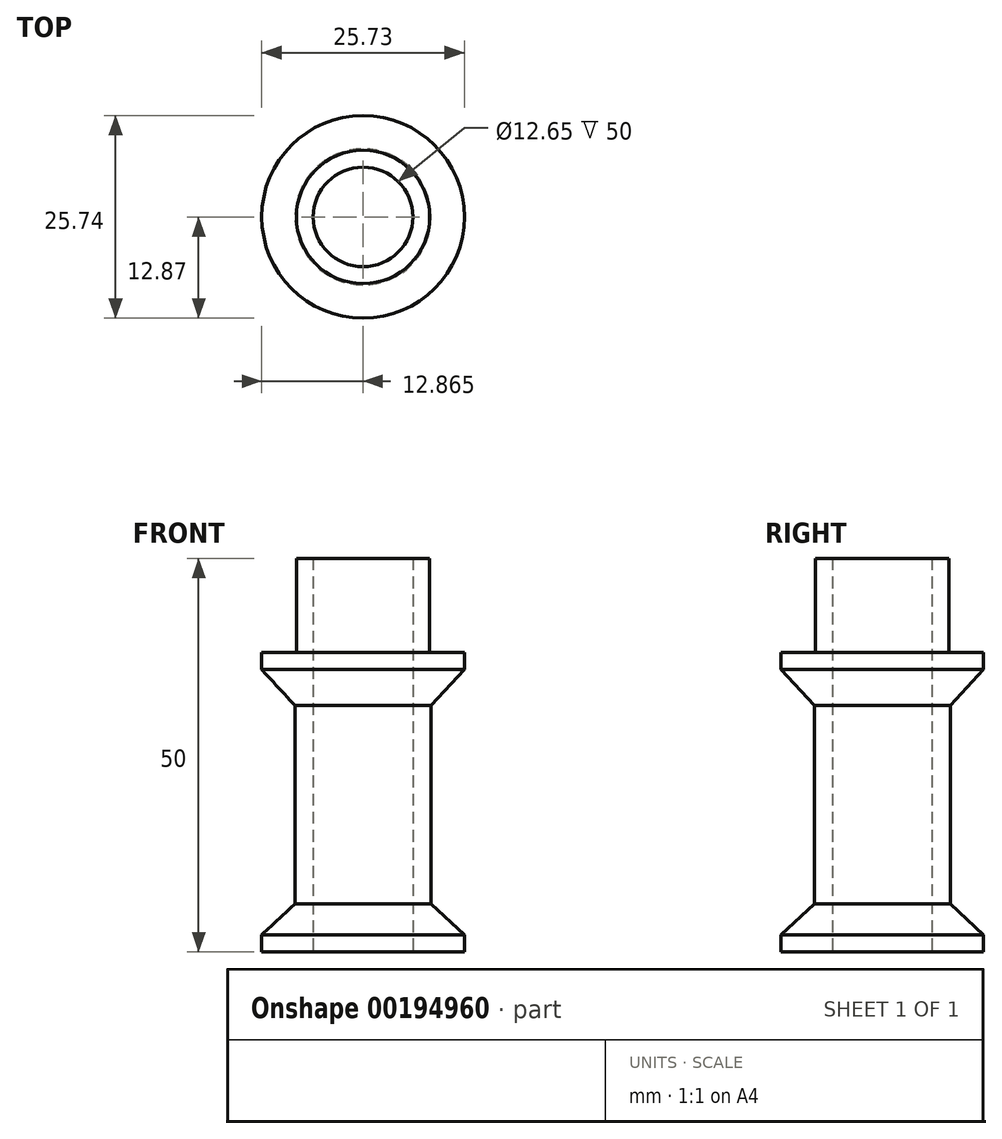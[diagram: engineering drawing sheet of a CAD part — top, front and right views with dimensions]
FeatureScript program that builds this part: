
annotation { "Feature Type Name" : "Feature", "Feature Type Description" : "" }
export const myFeature = defineFeature(function(context is Context, id is Id, definition is map)
    precondition{}
    {
        {
            var Q0;
            Q0=qCreatedBy(makeId("Front.planeOp"),FACE);
            var sketch = newSketch(context, id + "F0", { "sketchPlane" : qUnion([Q0])});
            skLineSegment(sketch, "E0", {"start": v(0, 0) * mm, "end": v(0, 50) * mm});
            skLineSegment(sketch, "E1", {"start": v(0, 50) * mm, "end": v(2.14, 50) * mm});
            skLineSegment(sketch, "E2", {"start": v(2.14, 50) * mm, "end": v(2.14, 38.07) * mm});
            skLineSegment(sketch, "E3", {"start": v(2.14, 38.07) * mm, "end": v(6.54, 38.07) * mm});
            skLineSegment(sketch, "E4", {"start": v(6.54, 38.07) * mm, "end": v(6.54, 35.87) * mm});
            skLineSegment(sketch, "E5", {"start": v(6.54, 35.87) * mm, "end": v(2.31, 31.3) * mm});
            skLineSegment(sketch, "E6", {"start": v(0, 0) * mm, "end": v(6.54, 0) * mm});
            skLineSegment(sketch, "E7", {"start": v(6.54, 0) * mm, "end": v(6.54, 2.18) * mm});
            skLineSegment(sketch, "E8", {"start": v(6.54, 2.18) * mm, "end": v(2.31, 6.1) * mm});
            skLineSegment(sketch, "E9", {"start": v(2.31, 31.3) * mm, "end": v(2.31, 6.1) * mm});
            skSolve(sketch);
        }
        {
            var Q0;
            Q0=qCreatedBy(makeId("Front.planeOp"),FACE);
            var sketch = newSketch(context, id + "F1", { "sketchPlane" : qUnion([Q0])});
            skLineSegment(sketch, "E10", {"start": v(0, 0) * mm, "end": v(-6.32, 0) * mm});
            skLineSegment(sketch, "E11", {"start": v(-6.33, 0) * mm, "end": v(-6.33, 3.97) * mm});
            skSolve(sketch);
        }
        {
            var Q0;
            Q0=makeQuery(id+"F0.imprint","IMPRINT",FACE,{"disambiguationData":[TD([[makeQuery(id+"F0.imprint","IMPRINT",EDGE,{"derivedFrom":sQuery(id+"F0.wireOp",EDGE,"E0")}),-1.0]])]});
            var Q1;
            Q1=sQuery(id+"F1.wireOp",EDGE,"E11");
            revolve(context, id + "F2", {"entities" : qUnion([Q0]), "axis" : qUnion([Q1]), "revolveType" : RevolveType.FULL});
        }
    });
